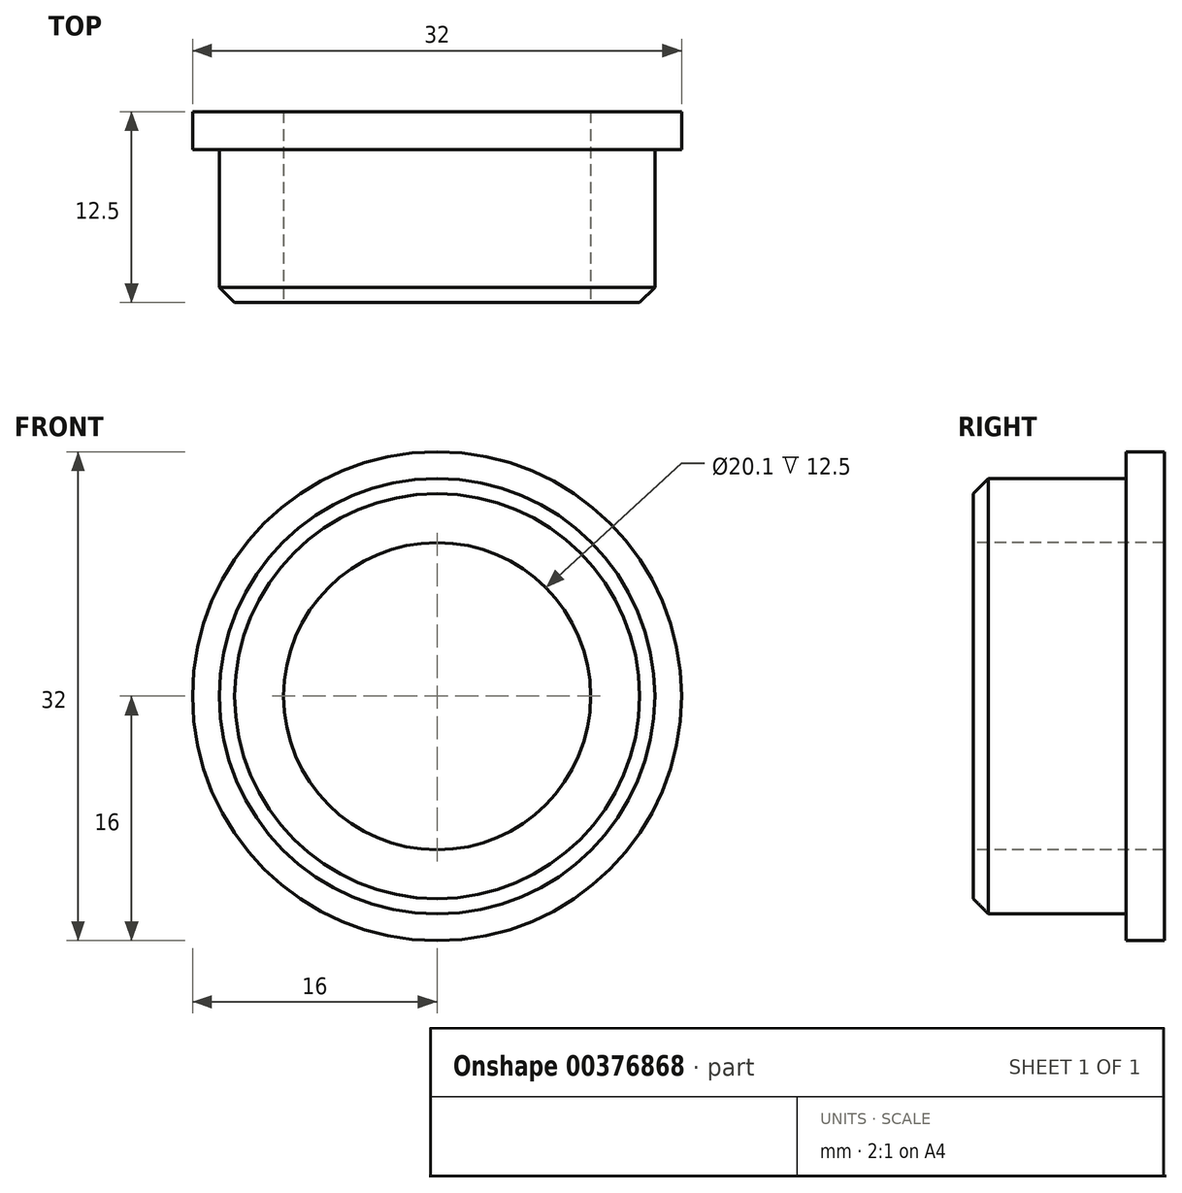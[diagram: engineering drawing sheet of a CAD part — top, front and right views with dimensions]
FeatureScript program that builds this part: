
annotation { "Feature Type Name" : "Feature", "Feature Type Description" : "" }
export const myFeature = defineFeature(function(context is Context, id is Id, definition is map)
    precondition{}
    {
        {
            var Q0;
            Q0=qCreatedBy(makeId("Front.planeOp"),FACE);
            var sketch = newSketch(context, id + "F0", { "sketchPlane" : qUnion([Q0])});
            skCircle(sketch, "E0", {"center": v(0, 0) * mm, "radius": 14.25 * mm});
            skSolve(sketch);
        }
        {
            var Q0;
            Q0=makeQuery(id+"F0.imprint","IMPRINT",FACE,{"disambiguationData":[TD([[makeQuery(id+"F0.imprint","IMPRINT",EDGE,{"derivedFrom":sQuery(id+"F0.wireOp",EDGE,"E0")}),1.0]])]});
            extrude(context, id + "F1", {"entities" : qUnion([Q0]), "depth" : 10 * mm});
        }
        {
            var Q0;
            Q0=qCreatedBy(makeId("Front.planeOp"),FACE);
            var sketch = newSketch(context, id + "F2", { "sketchPlane" : qUnion([Q0])});
            skCircle(sketch, "E1", {"center": v(0, 0) * mm, "radius": 16 * mm});
            skSolve(sketch);
        }
        {
            var Q0;
            Q0 = qSketchRegion(id + "F2", true);
            extrude(context, id + "F3", {"entities" : qUnion([Q0]), "operationType" : NewBodyOperationType.ADD, "oppositeDirection" : true, "depth" : 2.5 * mm});
        }
        {
            var Q0;
            Q0=makeQuery(id+"F1.opExtrude","CAP_EDGE",EDGE,{"disambiguationData":[OSD([sQuery(id+"F0.wireOp",EDGE,"E0")])],"isStart":false});
            chamfer(context, id + "F4", {"entities" : qUnion([Q0]), "width" : 1 * mm, "tangentPropagation" : true});
        }
        {
            var Q0;
            Q0=makeQuery(id+"F1.opExtrude","CAP_FACE",FACE,{"disambiguationData":[OSD([sQuery(id+"F0.wireOp",EDGE,"E0"),sQuery(id+"F0.wireOp",EDGE,"wFEfIrgv-n2wt-TdVd-5BYD-ljkVjt1gqXYO")])],"isStart":false});
            var sketch = newSketch(context, id + "F5", { "sketchPlane" : qUnion([Q0])});
            skCircle(sketch, "E2", {"center": v(0, 0) * mm, "radius": 10.05 * mm});
            skSolve(sketch);
        }
        {
            var Q0;
            Q0 = qSketchRegion(id + "F5", true);
            extrude(context, id + "F6", {"entities" : qUnion([Q0]), "operationType" : NewBodyOperationType.REMOVE, "oppositeDirection" : true, "depth" : 15 * mm});
        }
    });
